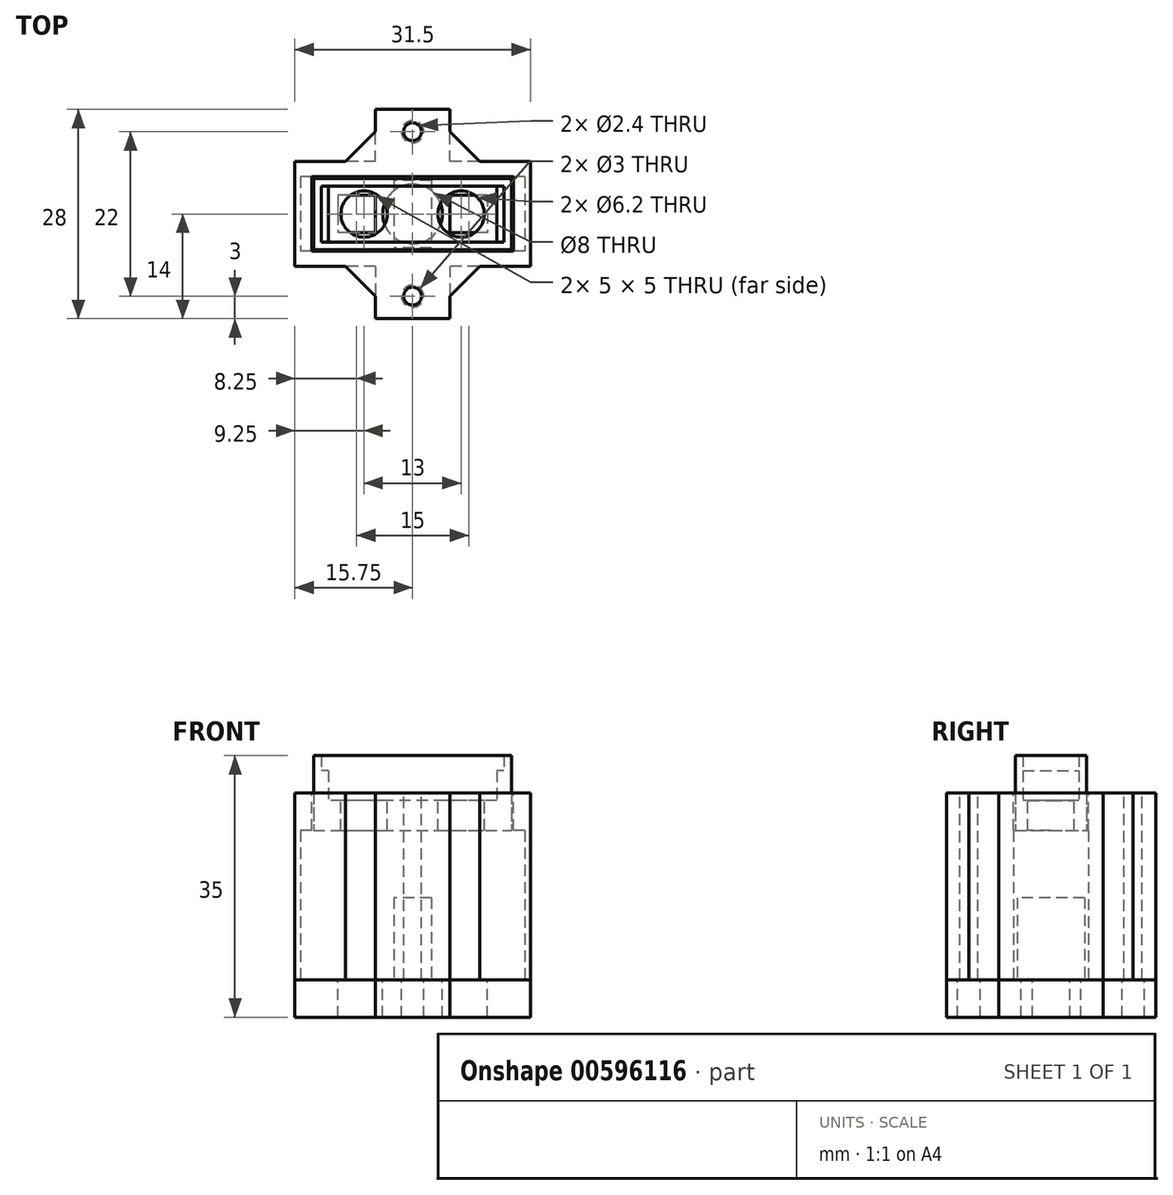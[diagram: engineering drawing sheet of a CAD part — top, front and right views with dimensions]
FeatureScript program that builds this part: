
annotation { "Feature Type Name" : "Feature", "Feature Type Description" : "" }
export const myFeature = defineFeature(function(context is Context, id is Id, definition is map)
    precondition{}
    {
        {
            var Q0;
            Q0=qCreatedBy(makeId("Top.planeOp"),FACE);
            var sketch = newSketch(context, id + "F0", { "sketchPlane" : qUnion([Q0])});
            skLineSegment(sketch, "E0.bottom", {"start": v(13.25, -4.75) * mm, "end": v(-13.25, -4.75) * mm});
            skLineSegment(sketch, "E0.top", {"start": v(13.25, 4.75) * mm, "end": v(-13.25, 4.75) * mm});
            skLineSegment(sketch, "E0.left", {"start": v(13.25, -4.75) * mm, "end": v(13.25, 4.75) * mm});
            skLineSegment(sketch, "E0.right", {"start": v(-13.25, -4.75) * mm, "end": v(-13.25, 4.75) * mm});
            skPoint(sketch, "E0.middle", {"position": v(0, 0) * mm});
            skSolve(sketch);
        }
        {
            var Q0;
            Q0=qSketchRegion(id+"F0",true);
            extrude(context, id + "F1", {"entities" : qUnion([Q0]), "depth" : 13 * mm, "offsetDistance" : 25 * mm});
        }
        {
            var Q0;
            Q0=makeQuery(id+"F1.opExtrude","CAP_FACE",FACE,{"disambiguationData":[OSD([sQuery(id+"F0.wireOp",EDGE,"E0.bottom"),sQuery(id+"F0.wireOp",EDGE,"E0.top"),sQuery(id+"F0.wireOp",EDGE,"E0.left"),sQuery(id+"F0.wireOp",EDGE,"E0.right")])],"isStart":false});
            var sketch = newSketch(context, id + "F2", { "sketchPlane" : qUnion([Q0])});
            skLineSegment(sketch, "E1.bottom", {"start": v(13.25, -4.75) * mm, "end": v(-13.25, -4.75) * mm});
            skLineSegment(sketch, "E1.top", {"start": v(13.25, 4.75) * mm, "end": v(-13.25, 4.75) * mm});
            skLineSegment(sketch, "E1.left", {"start": v(13.25, -4.75) * mm, "end": v(13.25, 4.75) * mm});
            skLineSegment(sketch, "E1.right", {"start": v(-13.25, -4.75) * mm, "end": v(-13.25, 4.75) * mm});
            skPoint(sketch, "E1.middle", {"position": v(0, 0) * mm});
            skLineSegment(sketch, "E2.bottom", {"start": v(12.25, -3.75) * mm, "end": v(-12.25, -3.75) * mm});
            skLineSegment(sketch, "E2.top", {"start": v(12.25, 3.75) * mm, "end": v(-12.25, 3.75) * mm});
            skLineSegment(sketch, "E2.left", {"start": v(12.25, -3.75) * mm, "end": v(12.25, 3.75) * mm});
            skLineSegment(sketch, "E2.right", {"start": v(-12.25, -3.75) * mm, "end": v(-12.25, 3.75) * mm});
            skSolve(sketch);
        }
        {
            var Q0;
            Q0=qSketchRegion(id+"F2",true);
            extrude(context, id + "F3", {"entities" : qUnion([Q0]), "operationType" : NewBodyOperationType.ADD, "depth" : 6 * mm, "offsetDistance" : 25 * mm});
        }
        {
            var Q0;
            Q0=makeQuery(id+"F1.opExtrude","CAP_FACE",FACE,{"disambiguationData":[OSD([sQuery(id+"F0.wireOp",EDGE,"E0.bottom"),sQuery(id+"F0.wireOp",EDGE,"E0.top"),sQuery(id+"F0.wireOp",EDGE,"E0.left"),sQuery(id+"F0.wireOp",EDGE,"E0.right")])],"isStart":false});
            var sketch = newSketch(context, id + "F4", { "sketchPlane" : qUnion([Q0])});
            skLineSegment(sketch, "E3.bottom", {"start": v(-12.25, 3.75) * mm, "end": v(-11.25, 3.75) * mm});
            skLineSegment(sketch, "E3.top", {"start": v(-12.25, -3.75) * mm, "end": v(-11.25, -3.75) * mm});
            skLineSegment(sketch, "E3.left", {"start": v(-12.25, 3.75) * mm, "end": v(-12.25, -3.75) * mm});
            skLineSegment(sketch, "E3.right", {"start": v(-11.25, 3.75) * mm, "end": v(-11.25, -3.75) * mm});
            skLineSegment(sketch, "E4.bottom", {"start": v(12.25, 3.75) * mm, "end": v(11.25, 3.75) * mm});
            skLineSegment(sketch, "E4.top", {"start": v(12.25, -3.75) * mm, "end": v(11.25, -3.75) * mm});
            skLineSegment(sketch, "E4.left", {"start": v(12.25, 3.75) * mm, "end": v(12.25, -3.75) * mm});
            skLineSegment(sketch, "E4.right", {"start": v(11.25, 3.75) * mm, "end": v(11.25, -3.75) * mm});
            skSolve(sketch);
        }
        {
            var Q0;
            Q0=qSketchRegion(id+"F4",true);
            extrude(context, id + "F5", {"entities" : qUnion([Q0]), "operationType" : NewBodyOperationType.ADD, "depth" : 4 * mm, "offsetDistance" : 25 * mm});
        }
        {
            var Q0;
            Q0=makeQuery(id+"F1.opExtrude","CAP_FACE",FACE,{"disambiguationData":[OSD([sQuery(id+"F0.wireOp",EDGE,"E0.bottom"),sQuery(id+"F0.wireOp",EDGE,"E0.top"),sQuery(id+"F0.wireOp",EDGE,"E0.left"),sQuery(id+"F0.wireOp",EDGE,"E0.right")])],"isStart":false});
            var sketch = newSketch(context, id + "F6", { "sketchPlane" : qUnion([Q0])});
            skCircle(sketch, "E5", {"center": v(-6.5, 0) * mm, "radius": 3.1 * mm});
            skCircle(sketch, "E6", {"center": v(6.5, 0) * mm, "radius": 3.1 * mm});
            skSolve(sketch);
        }
        {
            var Q0;
            Q0=qSketchRegion(id+"F6",true);
            extrude(context, id + "F7", {"entities" : qUnion([Q0]), "operationType" : NewBodyOperationType.REMOVE, "oppositeDirection" : true, "depth" : 19 * mm, "offsetDistance" : 25 * mm});
        }
        {
            var Q0;
            Q0=makeQuery(id+"F1.opExtrude","CAP_FACE",FACE,{"disambiguationData":[OSD([sQuery(id+"F0.wireOp",EDGE,"E0.bottom"),sQuery(id+"F0.wireOp",EDGE,"E0.top"),sQuery(id+"F0.wireOp",EDGE,"E0.left"),sQuery(id+"F0.wireOp",EDGE,"E0.right")])],"isStart":true});
            var sketch = newSketch(context, id + "F8", { "sketchPlane" : qUnion([Q0])});
            skLineSegment(sketch, "E7.bottom", {"start": v(-13.25, -4.75) * mm, "end": v(-14.75, -4.75) * mm});
            skLineSegment(sketch, "E7.top", {"start": v(-13.25, 4.75) * mm, "end": v(-14.75, 4.75) * mm});
            skLineSegment(sketch, "E7.left", {"start": v(-13.25, -4.75) * mm, "end": v(-13.25, 4.75) * mm});
            skLineSegment(sketch, "E7.right", {"start": v(-14.75, -4.75) * mm, "end": v(-14.75, 4.75) * mm});
            skLineSegment(sketch, "E8.bottom", {"start": v(13.25, -4.75) * mm, "end": v(14.75, -4.75) * mm});
            skLineSegment(sketch, "E8.top", {"start": v(13.25, 4.75) * mm, "end": v(14.75, 4.75) * mm});
            skLineSegment(sketch, "E8.left", {"start": v(13.25, -4.75) * mm, "end": v(13.25, 4.75) * mm});
            skLineSegment(sketch, "E8.right", {"start": v(14.75, -4.75) * mm, "end": v(14.75, 4.75) * mm});
            skSolve(sketch);
        }
        {
            var Q0;
            Q0=qSketchRegion(id+"F8",true);
            extrude(context, id + "F9", {"entities" : qUnion([Q0]), "operationType" : NewBodyOperationType.ADD, "oppositeDirection" : true, "depth" : 9 * mm, "offsetDistance" : 25 * mm});
        }
        {
            var Q0;
            Q0=makeQuery(id+"F9.boolean.opBoolean","MERGE",FACE,{"derivedFrom":[makeQuery(id+"F1.opExtrude","CAP_FACE",FACE,{"disambiguationData":[OSD([sQuery(id+"F0.wireOp",EDGE,"E0.bottom"),sQuery(id+"F0.wireOp",EDGE,"E0.top"),sQuery(id+"F0.wireOp",EDGE,"E0.left"),sQuery(id+"F0.wireOp",EDGE,"E0.right")])],"isStart":true}),makeQuery(id+"F9.opExtrude","CAP_FACE",FACE,{"disambiguationData":[OSD([sQuery(id+"F8.wireOp",EDGE,"E7.bottom"),sQuery(id+"F8.wireOp",EDGE,"E7.top"),sQuery(id+"F8.wireOp",EDGE,"E7.left"),sQuery(id+"F8.wireOp",EDGE,"E7.right")])],"isStart":true}),makeQuery(id+"F9.opExtrude","CAP_FACE",FACE,{"disambiguationData":[OSD([sQuery(id+"F8.wireOp",EDGE,"E8.bottom"),sQuery(id+"F8.wireOp",EDGE,"E8.top"),sQuery(id+"F8.wireOp",EDGE,"E8.left"),sQuery(id+"F8.wireOp",EDGE,"E8.right")])],"isStart":true})]});
            var sketch = newSketch(context, id + "F10", { "sketchPlane" : qUnion([Q0])});
            skCircle(sketch, "E9", {"center": v(0, 0) * mm, "radius": 2.55 * mm});
            skSolve(sketch);
        }
        {
            var Q0;
            Q0=qSketchRegion(id+"F10",true);
            extrude(context, id + "F11", {"entities" : qUnion([Q0]), "operationType" : NewBodyOperationType.REMOVE, "oppositeDirection" : true, "depth" : 3 * mm, "offsetDistance" : 25 * mm});
        }
        {
            var Q0;
            Q0=qCreatedBy(makeId("Top.planeOp"),FACE);
            cPlane(context, id + "F12", {"entities" : qUnion([Q0]), "cplaneType" : CPlaneType.OFFSET, "offset" : 14 * mm, "width" : 150 * mm, "height" : 150 * mm});
        }
        {
            var Q0;
            Q0=qCreatedBy(id+"F12.planeOp",FACE);
            var sketch = newSketch(context, id + "F13", { "sketchPlane" : qUnion([Q0])});
            skLineSegment(sketch, "E10.bottom", {"start": v(15.75, -7) * mm, "end": v(-15.75, -7) * mm});
            skLineSegment(sketch, "E10.top", {"start": v(15.75, 7) * mm, "end": v(-15.75, 7) * mm});
            skLineSegment(sketch, "E10.left", {"start": v(15.75, -7) * mm, "end": v(15.75, 7) * mm});
            skLineSegment(sketch, "E10.right", {"start": v(-15.75, -7) * mm, "end": v(-15.75, 7) * mm});
            skPoint(sketch, "E10.middle", {"position": v(0, 0) * mm});
            skLineSegment(sketch, "E11.bottom", {"start": v(-5, 7) * mm, "end": v(5, 7) * mm});
            skLineSegment(sketch, "E11.top", {"start": v(-5, 14) * mm, "end": v(5, 14) * mm});
            skLineSegment(sketch, "E11.left", {"start": v(-5, 7) * mm, "end": v(-5, 14) * mm});
            skLineSegment(sketch, "E11.right", {"start": v(5, 7) * mm, "end": v(5, 14) * mm});
            skLineSegment(sketch, "E12.bottom", {"start": v(-5, -7) * mm, "end": v(5, -7) * mm});
            skLineSegment(sketch, "E12.top", {"start": v(-5, -14) * mm, "end": v(5, -14) * mm});
            skLineSegment(sketch, "E12.left", {"start": v(-5, -7) * mm, "end": v(-5, -14) * mm});
            skLineSegment(sketch, "E12.right", {"start": v(5, -7) * mm, "end": v(5, -14) * mm});
            skLineSegment(sketch, "E13.bottom", {"start": v(13.5, -5) * mm, "end": v(-13.5, -5) * mm});
            skLineSegment(sketch, "E13.top", {"start": v(13.5, 5) * mm, "end": v(-13.5, 5) * mm});
            skLineSegment(sketch, "E13.left", {"start": v(13.5, -5) * mm, "end": v(13.5, 5) * mm});
            skLineSegment(sketch, "E13.right", {"start": v(-13.5, -5) * mm, "end": v(-13.5, 5) * mm});
            skSolve(sketch);
        }
        {
            var Q0;
            Q0=qSketchRegion(id+"F13",true);
            extrude(context, id + "F14", {"entities" : qUnion([Q0]), "oppositeDirection" : true, "depth" : 25 * mm, "offsetDistance" : 25 * mm});
        }
        {
            var Q0;
            Q0=makeQuery(id+"F14.opExtrude","CAP_FACE",FACE,{"disambiguationData":[OSD([sQuery(id+"F13.wireOp",EDGE,"E10.bottom"),sQuery(id+"F13.wireOp",EDGE,"E10.top"),sQuery(id+"F13.wireOp",EDGE,"E10.left"),sQuery(id+"F13.wireOp",EDGE,"E10.right"),sQuery(id+"F13.wireOp",EDGE,"E11.top"),sQuery(id+"F13.wireOp",EDGE,"E11.left"),sQuery(id+"F13.wireOp",EDGE,"E11.right"),sQuery(id+"F13.wireOp",EDGE,"E12.top"),sQuery(id+"F13.wireOp",EDGE,"E12.left"),sQuery(id+"F13.wireOp",EDGE,"E12.right")])],"isStart":false});
            var sketch = newSketch(context, id + "F15", { "sketchPlane" : qUnion([Q0])});
            skLineSegment(sketch, "E14.bottom", {"start": v(15, -5) * mm, "end": v(-15, -5) * mm});
            skLineSegment(sketch, "E14.top", {"start": v(15, 5) * mm, "end": v(-15, 5) * mm});
            skLineSegment(sketch, "E14.left", {"start": v(15, -5) * mm, "end": v(15, 5) * mm});
            skLineSegment(sketch, "E14.right", {"start": v(-15, -5) * mm, "end": v(-15, 5) * mm});
            skPoint(sketch, "E14.middle", {"position": v(0, 0) * mm});
            skSolve(sketch);
        }
        {
            var Q0;
            Q0=qSketchRegion(id+"F15",true);
            extrude(context, id + "F16", {"entities" : qUnion([Q0]), "operationType" : NewBodyOperationType.REMOVE, "oppositeDirection" : true, "depth" : 20 * mm, "offsetDistance" : 25 * mm});
        }
        {
            var Q0;
            Q0=makeQuery(id+"F14.opExtrude","CAP_FACE",FACE,{"disambiguationData":[OSD([sQuery(id+"F13.wireOp",EDGE,"E10.bottom"),sQuery(id+"F13.wireOp",EDGE,"E10.top"),sQuery(id+"F13.wireOp",EDGE,"E10.left"),sQuery(id+"F13.wireOp",EDGE,"E10.right"),sQuery(id+"F13.wireOp",EDGE,"E11.top"),sQuery(id+"F13.wireOp",EDGE,"E11.left"),sQuery(id+"F13.wireOp",EDGE,"E11.right"),sQuery(id+"F13.wireOp",EDGE,"E12.top"),sQuery(id+"F13.wireOp",EDGE,"E12.left"),sQuery(id+"F13.wireOp",EDGE,"E12.right")])],"isStart":true});
            var sketch = newSketch(context, id + "F17", { "sketchPlane" : qUnion([Q0])});
            skCircle(sketch, "E15", {"center": v(0, 11) * mm, "radius": 1.2 * mm});
            skCircle(sketch, "E16", {"center": v(0, -11) * mm, "radius": 1.2 * mm});
            skSolve(sketch);
        }
        {
            var Q0;
            Q0=qSketchRegion(id+"F17",true);
            extrude(context, id + "F18", {"entities" : qUnion([Q0]), "operationType" : NewBodyOperationType.REMOVE, "oppositeDirection" : true, "depth" : 25 * mm, "offsetDistance" : 25 * mm});
        }
        {
            var Q0;
            Q0=makeQuery(id+"F14.opExtrude","CAP_FACE",FACE,{"disambiguationData":[OSD([sQuery(id+"F13.wireOp",EDGE,"E10.bottom"),sQuery(id+"F13.wireOp",EDGE,"E10.top"),sQuery(id+"F13.wireOp",EDGE,"E10.left"),sQuery(id+"F13.wireOp",EDGE,"E10.right"),sQuery(id+"F13.wireOp",EDGE,"E11.top"),sQuery(id+"F13.wireOp",EDGE,"E11.left"),sQuery(id+"F13.wireOp",EDGE,"E11.right"),sQuery(id+"F13.wireOp",EDGE,"E12.top"),sQuery(id+"F13.wireOp",EDGE,"E12.left"),sQuery(id+"F13.wireOp",EDGE,"E12.right"),sQuery(id+"F13.wireOp",EDGE,"E13.bottom"),sQuery(id+"F13.wireOp",EDGE,"E13.top"),sQuery(id+"F13.wireOp",EDGE,"E13.left"),sQuery(id+"F13.wireOp",EDGE,"E13.right")])],"isStart":false});
            var sketch = newSketch(context, id + "F19", { "sketchPlane" : qUnion([Q0])});
            skLineSegment(sketch, "E17.bottom", {"start": v(15.75, -7) * mm, "end": v(-15.75, -7) * mm});
            skLineSegment(sketch, "E17.top", {"start": v(15.75, 7) * mm, "end": v(-15.75, 7) * mm});
            skLineSegment(sketch, "E17.left", {"start": v(15.75, -7) * mm, "end": v(15.75, 7) * mm});
            skLineSegment(sketch, "E17.right", {"start": v(-15.75, -7) * mm, "end": v(-15.75, 7) * mm});
            skPoint(sketch, "E17.middle", {"position": v(0, 0) * mm});
            skLineSegment(sketch, "E18.bottom", {"start": v(-5, 7) * mm, "end": v(5, 7) * mm});
            skLineSegment(sketch, "E18.top", {"start": v(-5, 14) * mm, "end": v(5, 14) * mm});
            skLineSegment(sketch, "E18.left", {"start": v(-5, 7) * mm, "end": v(-5, 14) * mm});
            skLineSegment(sketch, "E18.right", {"start": v(5, 7) * mm, "end": v(5, 14) * mm});
            skLineSegment(sketch, "E19.bottom", {"start": v(5, -7) * mm, "end": v(-5, -7) * mm});
            skLineSegment(sketch, "E19.top", {"start": v(5, -14) * mm, "end": v(-5, -14) * mm});
            skLineSegment(sketch, "E19.left", {"start": v(5, -7) * mm, "end": v(5, -14) * mm});
            skLineSegment(sketch, "E19.right", {"start": v(-5, -7) * mm, "end": v(-5, -14) * mm});
            skCircle(sketch, "E20", {"center": v(0, 0) * mm, "radius": 4 * mm});
            skLineSegment(sketch, "E21.bottom", {"start": v(-5, -2.5) * mm, "end": v(-10, -2.5) * mm});
            skLineSegment(sketch, "E21.top", {"start": v(-5, 2.5) * mm, "end": v(-10, 2.5) * mm});
            skLineSegment(sketch, "E21.left", {"start": v(-5, -2.5) * mm, "end": v(-5, 2.5) * mm});
            skLineSegment(sketch, "E21.right", {"start": v(-10, -2.5) * mm, "end": v(-10, 2.5) * mm});
            skPoint(sketch, "E21.middle", {"position": v(-7.5, 0) * mm});
            skLineSegment(sketch, "E22.bottom", {"start": v(10, -2.5) * mm, "end": v(5, -2.5) * mm});
            skLineSegment(sketch, "E22.top", {"start": v(10, 2.5) * mm, "end": v(5, 2.5) * mm});
            skLineSegment(sketch, "E22.left", {"start": v(10, -2.5) * mm, "end": v(10, 2.5) * mm});
            skLineSegment(sketch, "E22.right", {"start": v(5, -2.5) * mm, "end": v(5, 2.5) * mm});
            skPoint(sketch, "E22.middle", {"position": v(7.5, 0) * mm});
            skCircle(sketch, "E23", {"center": v(0, 11) * mm, "radius": 1.5 * mm});
            skCircle(sketch, "E24", {"center": v(0, -11) * mm, "radius": 1.5 * mm});
            skSolve(sketch);
        }
        {
            var Q0;
            Q0=qSketchRegion(id+"F19",true);
            extrude(context, id + "F20", {"entities" : qUnion([Q0]), "depth" : 5 * mm, "offsetDistance" : 25 * mm});
        }
        {
            var Q0;
            Q0=makeQuery(id+"F14.opExtrude","SWEPT_EDGE",EDGE,{"disambiguationData":[OSD([sQuery(id+"F13.wireOp",EDGE,"E10.top"),sQuery(id+"F13.wireOp",EDGE,"E11.bottom"),sQuery(id+"F13.wireOp",EDGE,"E11.left")])]});
            var Q1;
            Q1=makeQuery(id+"F14.opExtrude","SWEPT_EDGE",EDGE,{"disambiguationData":[OSD([sQuery(id+"F13.wireOp",EDGE,"E10.top"),sQuery(id+"F13.wireOp",EDGE,"E11.bottom"),sQuery(id+"F13.wireOp",EDGE,"E11.right")])]});
            var Q2;
            Q2=makeQuery(id+"F14.opExtrude","SWEPT_EDGE",EDGE,{"disambiguationData":[OSD([sQuery(id+"F13.wireOp",EDGE,"E10.bottom"),sQuery(id+"F13.wireOp",EDGE,"E12.bottom"),sQuery(id+"F13.wireOp",EDGE,"E12.right")])]});
            var Q3;
            Q3=makeQuery(id+"F14.opExtrude","SWEPT_EDGE",EDGE,{"disambiguationData":[OSD([sQuery(id+"F13.wireOp",EDGE,"E10.bottom"),sQuery(id+"F13.wireOp",EDGE,"E12.bottom"),sQuery(id+"F13.wireOp",EDGE,"E12.left")])]});
            chamfer(context, id + "F21", {"entities" : qUnion([Q0, Q1, Q2, Q3]), "width" : 4 * mm, "tangentPropagation" : true});
        }
        {
            var Q0;
            Q0=makeQuery(id+"F14.opExtrude","CAP_FACE",FACE,{"disambiguationData":[OSD([sQuery(id+"F13.wireOp",EDGE,"E10.bottom"),sQuery(id+"F13.wireOp",EDGE,"E10.top"),sQuery(id+"F13.wireOp",EDGE,"E10.left"),sQuery(id+"F13.wireOp",EDGE,"E10.right"),sQuery(id+"F13.wireOp",EDGE,"E11.top"),sQuery(id+"F13.wireOp",EDGE,"E11.left"),sQuery(id+"F13.wireOp",EDGE,"E11.right"),sQuery(id+"F13.wireOp",EDGE,"E12.top"),sQuery(id+"F13.wireOp",EDGE,"E12.left"),sQuery(id+"F13.wireOp",EDGE,"E12.right"),sQuery(id+"F13.wireOp",EDGE,"E13.bottom"),sQuery(id+"F13.wireOp",EDGE,"E13.top"),sQuery(id+"F13.wireOp",EDGE,"E13.left"),sQuery(id+"F13.wireOp",EDGE,"E13.right")])],"isStart":false});
            cPlane(context, id + "F22", {"entities" : qUnion([Q0]), "cplaneType" : CPlaneType.OFFSET, "offset" : 0 * mm, "width" : 150 * mm, "height" : 150 * mm});
        }
        {
            var Q0;
            Q0=qCreatedBy(id+"F22.planeOp",FACE);
            var sketch = newSketch(context, id + "F23", { "sketchPlane" : qUnion([Q0])});
            skLineSegment(sketch, "E25.bottom", {"start": v(2.5, -4.5) * mm, "end": v(-2.5, -4.5) * mm});
            skLineSegment(sketch, "E25.top", {"start": v(2.5, 4.5) * mm, "end": v(-2.5, 4.5) * mm});
            skLineSegment(sketch, "E25.left", {"start": v(2.5, -4.5) * mm, "end": v(2.5, 4.5) * mm});
            skLineSegment(sketch, "E25.right", {"start": v(-2.5, -4.5) * mm, "end": v(-2.5, 4.5) * mm});
            skPoint(sketch, "E25.middle", {"position": v(0, 0) * mm});
            skLineSegment(sketch, "E26.0", {"start": v(15, 5) * mm, "end": v(-15, 5) * mm});
            skLineSegment(sketch, "E26.1", {"start": v(15, -5) * mm, "end": v(-15, -5) * mm});
            skPoint(sketch, "E27", {"position": v(0, 5) * mm});
            skSolve(sketch);
        }
        {
            var Q0;
            Q0=qSketchRegion(id+"F23",true);
            extrude(context, id + "F24", {"entities" : qUnion([Q0]), "oppositeDirection" : true, "depth" : 11 * mm, "offsetDistance" : 25 * mm});
        }
    });
